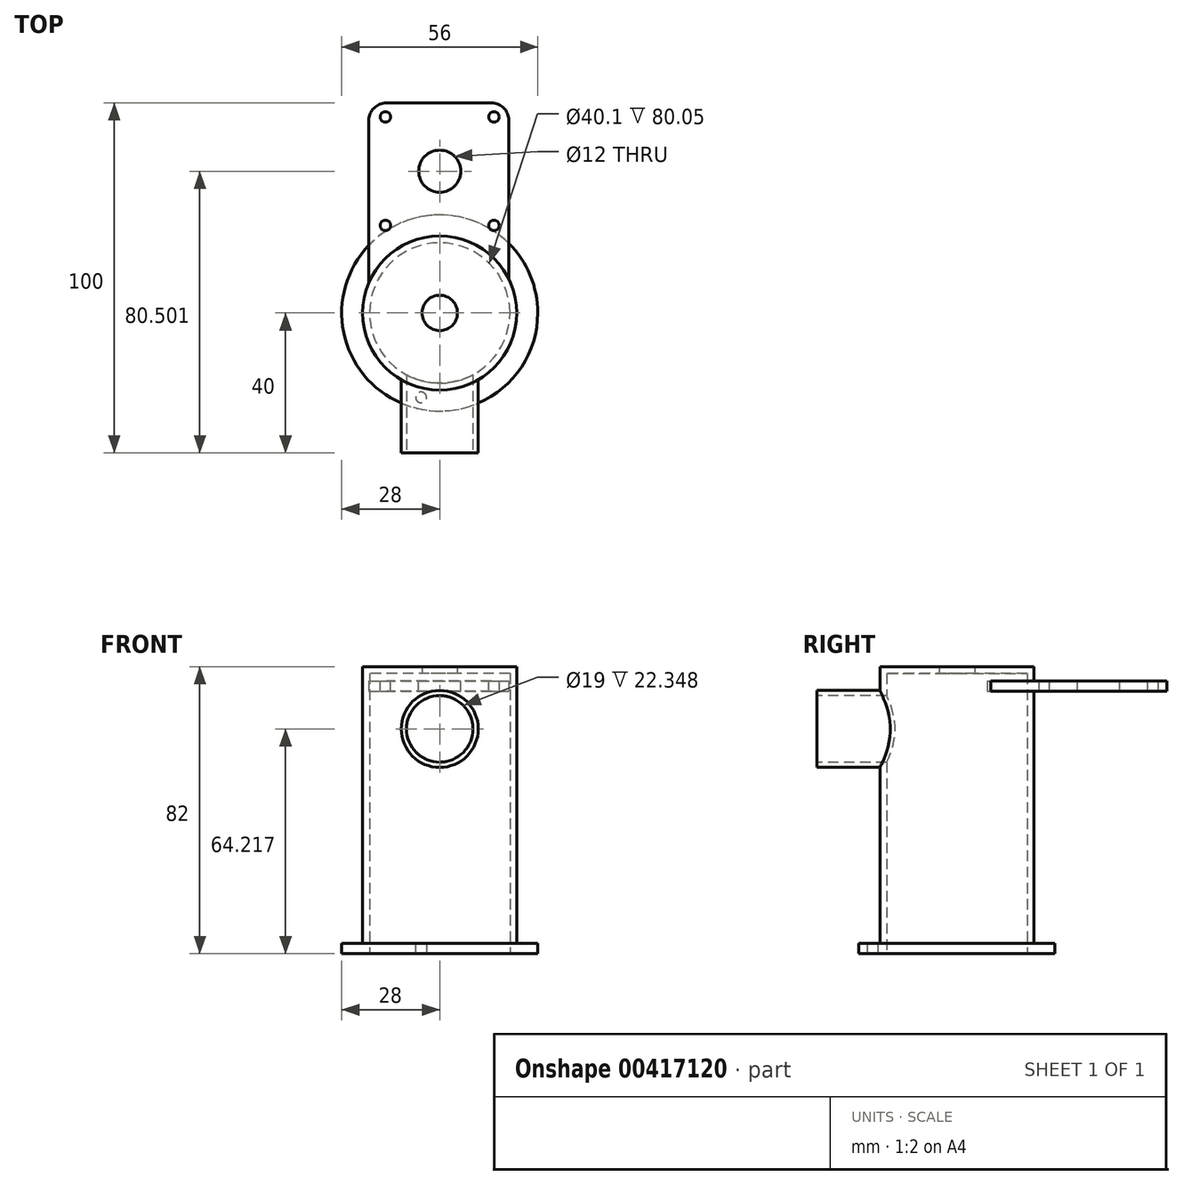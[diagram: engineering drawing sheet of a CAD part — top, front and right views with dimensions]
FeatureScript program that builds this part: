
annotation { "Feature Type Name" : "Feature", "Feature Type Description" : "" }
export const myFeature = defineFeature(function(context is Context, id is Id, definition is map)
    precondition{}
    {
        {
            var Q0;
            Q0=qCreatedBy(makeId("Top.planeOp"),FACE);
            var sketch = newSketch(context, id + "F0", { "sketchPlane" : qUnion([Q0])});
            skCircle(sketch, "E0", {"center": v(0, 0) * mm, "radius": 22 * mm});
            skCircle(sketch, "E1", {"center": v(0, 0) * mm, "radius": 28 * mm});
            skSolve(sketch);
        }
        {
            var Q0;
            Q0=makeQuery(id+"F0.imprint","IMPRINT",FACE,{"disambiguationData":[TD([[makeQuery(id+"F0.imprint","IMPRINT",EDGE,{"derivedFrom":sQuery(id+"F0.wireOp",EDGE,"E0")}),1.0]])]});
            extrude(context, id + "F1", {"entities" : qUnion([Q0]), "depth" : 82 * mm});
        }
        {
            var Q0;
            Q0=makeQuery(id+"F1.opExtrude","CAP_FACE",FACE,{"disambiguationData":[OSD([sQuery(id+"F0.wireOp",EDGE,"E0")])],"isStart":true});
            shell(context, id + "F2", {"entities" : qUnion([Q0]), "thickness" : 1.95 * mm});
        }
        {
            var Q0;
            Q0=makeQuery(id+"F0.imprint","IMPRINT",FACE,{"disambiguationData":[TD([[makeQuery(id+"F0.imprint","IMPRINT",EDGE,{"derivedFrom":sQuery(id+"F0.wireOp",EDGE,"E0")}),-1.0]])]});
            extrude(context, id + "F3", {"entities" : qUnion([Q0]), "operationType" : NewBodyOperationType.ADD, "depth" : 3 * mm});
        }
        {
            var Q0;
            Q0=qCreatedBy(makeId("Front.planeOp"),FACE);
            var sketch = newSketch(context, id + "F4", { "sketchPlane" : qUnion([Q0])});
            skLineSegment(sketch, "E2", {"start": v(0, -30.48) * mm, "end": v(0, 118.91) * mm, "construction": true});
            skSolve(sketch);
        }
        {
            var Q0;
            Q0=qCreatedBy(makeId("Top.planeOp"),FACE);
            var sketch = newSketch(context, id + "F5", { "sketchPlane" : qUnion([Q0])});
            skCircle(sketch, "E3", {"center": v(0, 0) * mm, "radius": 5.05 * mm});
            skSolve(sketch);
        }
        {
            var Q0;
            Q0 = qSketchRegion(id + "F5", true);
            extrude(context, id + "F6", {"entities" : qUnion([Q0]), "operationType" : NewBodyOperationType.REMOVE, "depth" : 90 * mm});
        }
        {
            var Q0;
            Q0=makeQuery(id+"F0.imprint","IMPRINT",FACE,{"disambiguationData":[TD([[makeQuery(id+"F0.imprint","IMPRINT",EDGE,{"derivedFrom":sQuery(id+"F0.wireOp",EDGE,"E0")}),-1.0]])]});
            var sketch = newSketch(context, id + "F7", { "sketchPlane" : qUnion([Q0])});
            skCircle(sketch, "E4", {"center": v(-5.33, -24.1) * mm, "radius": 1.55 * mm});
            skSolve(sketch);
        }
        {
            var Q0;
            Q0 = qSketchRegion(id + "F7", true);
            extrude(context, id + "F8", {"entities" : qUnion([Q0]), "operationType" : NewBodyOperationType.REMOVE, "depth" : 5 * mm});
        }
        {
            var Q0;
            Q0=qCreatedBy(makeId("Front.planeOp"),FACE);
            cPlane(context, id + "F9", {"entities" : qUnion([Q0]), "cplaneType" : CPlaneType.OFFSET, "offset" : 40 * mm, "width" : 150 * mm, "height" : 150 * mm});
        }
        {
            var Q0;
            Q0=qCreatedBy(id+"F9.planeOp",FACE);
            var sketch = newSketch(context, id + "F10", { "sketchPlane" : qUnion([Q0])});
            skCircle(sketch, "E5", {"center": v(0, 64.22) * mm, "radius": 11 * mm});
            skSolve(sketch);
        }
        {
            var Q0;
            Q0=makeQuery(id+"F10.imprint","IMPRINT",FACE,{"disambiguationData":[TD([[makeQuery(id+"F10.imprint","IMPRINT",EDGE,{"derivedFrom":sQuery(id+"F10.wireOp",EDGE,"E5")}),1.0]])]});
            extrude(context, id + "F11", {"entities" : qUnion([Q0]), "operationType" : NewBodyOperationType.ADD, "endBound" : BoundingType.UP_TO_NEXT, "oppositeDirection" : true, "depth" : 25 * mm});
        }
        {
            var Q0;
            Q0=makeQuery(id+"F11.opExtrude","CAP_FACE",FACE,{"disambiguationData":[OSD([sQuery(id+"F10.wireOp",EDGE,"E5")])],"isStart":true});
            var sketch = newSketch(context, id + "F12", { "sketchPlane" : qUnion([Q0])});
            skCircle(sketch, "E6", {"center": v(0, 64.22) * mm, "radius": 9.5 * mm});
            skSolve(sketch);
        }
        {
            var Q0;
            Q0 = qSketchRegion(id + "F12", true);
            extrude(context, id + "F13", {"entities" : qUnion([Q0]), "operationType" : NewBodyOperationType.REMOVE, "oppositeDirection" : true, "depth" : 30 * mm});
        }
        {
            var Q0;
            Q0=qCreatedBy(makeId("Front.planeOp"),FACE);
            cPlane(context, id + "F14", {"entities" : qUnion([Q0]), "cplaneType" : CPlaneType.OFFSET, "offset" : 60 * mm, "oppositeDirection" : true, "width" : 150 * mm, "height" : 150 * mm});
        }
        {
            var Q0;
            Q0=qCreatedBy(id+"F14.planeOp",FACE);
            var sketch = newSketch(context, id + "F15", { "sketchPlane" : qUnion([Q0])});
            skLineSegment(sketch, "E7.bottom", {"start": v(19.76, 74.93) * mm, "end": v(-20.24, 74.93) * mm});
            skLineSegment(sketch, "E7.top", {"start": v(19.76, 77.93) * mm, "end": v(-20.24, 77.93) * mm});
            skLineSegment(sketch, "E7.left", {"start": v(19.76, 74.93) * mm, "end": v(19.76, 77.93) * mm});
            skLineSegment(sketch, "E7.right", {"start": v(-20.24, 74.93) * mm, "end": v(-20.24, 77.93) * mm});
            skSolve(sketch);
        }
        {
            var Q0;
            Q0 = qSketchRegion(id + "F15", true);
            extrude(context, id + "F16", {"entities" : qUnion([Q0]), "operationType" : NewBodyOperationType.ADD, "endBound" : BoundingType.UP_TO_NEXT, "depth" : 25 * mm});
        }
        {
            var Q0;
            Q0=makeQuery(id+"F1.opExtrude","CAP_FACE",FACE,{"disambiguationData":[OSD([sQuery(id+"F0.wireOp",EDGE,"E0")])],"isStart":false});
            var sketch = newSketch(context, id + "F17", { "sketchPlane" : qUnion([Q0])});
            skLineSegment(sketch, "E8", {"start": v(0, 40.5) * mm, "end": v(0, 0) * mm, "construction": true});
            skLineSegment(sketch, "E9", {"start": v(-19.3, 21.76) * mm, "end": v(18.59, 59.64) * mm, "construction": true});
            skLineSegment(sketch, "E10.bottom", {"start": v(15.5, 25) * mm, "end": v(-15.5, 25) * mm});
            skLineSegment(sketch, "E10.top", {"start": v(15.5, 56) * mm, "end": v(-15.5, 56) * mm});
            skLineSegment(sketch, "E10.left", {"start": v(15.5, 25) * mm, "end": v(15.5, 56) * mm});
            skLineSegment(sketch, "E10.right", {"start": v(-15.5, 25) * mm, "end": v(-15.5, 56) * mm});
            skPoint(sketch, "E10.middle", {"position": v(0, 40.5) * mm});
            skCircle(sketch, "E11", {"center": v(-15.5, 56) * mm, "radius": 1.5 * mm});
            skCircle(sketch, "E12", {"center": v(15.5, 56) * mm, "radius": 1.5 * mm});
            skCircle(sketch, "E13", {"center": v(-15.5, 25) * mm, "radius": 1.5 * mm});
            skCircle(sketch, "E14", {"center": v(15.5, 25) * mm, "radius": 1.5 * mm});
            skCircle(sketch, "E15", {"center": v(0, 40.5) * mm, "radius": 6 * mm});
            skSolve(sketch);
        }
        {
            var Q0;
            {var subQ0=sQuery(id+"F17.wireOp",EDGE,"E10.left");var subQ1=sQuery(id+"F17.wireOp",EDGE,"E10.top");var subQ2=makeQuery(id+"F17.imprint","INTERSECT",VERTEX,{"derivedFrom":[subQ1,subQ0]});Q0=makeQuery(id+"F17.imprint","IMPRINT",FACE,{"disambiguationData":[TD([[makeQuery(id+"F17.imprint","IMPRINT",EDGE,{"disambiguationData":[TD([[subQ2,-1.0]])],"derivedFrom":subQ1}),-1.0]])]});}
            var Q1;
            {var subQ0=sQuery(id+"F17.wireOp",EDGE,"E10.left");var subQ1=sQuery(id+"F17.wireOp",EDGE,"E10.top");var subQ2=makeQuery(id+"F17.imprint","INTERSECT",VERTEX,{"derivedFrom":[subQ1,subQ0]});Q1=makeQuery(id+"F17.imprint","IMPRINT",FACE,{"disambiguationData":[TD([[makeQuery(id+"F17.imprint","IMPRINT",EDGE,{"disambiguationData":[TD([[subQ2,-1.0]])],"derivedFrom":subQ1}),1.0]])]});}
            var Q2;
            {var subQ0=sQuery(id+"F17.wireOp",EDGE,"E10.right");var subQ1=sQuery(id+"F17.wireOp",EDGE,"E10.top");var subQ2=makeQuery(id+"F17.imprint","INTERSECT",VERTEX,{"derivedFrom":[subQ1,subQ0]});Q2=makeQuery(id+"F17.imprint","IMPRINT",FACE,{"disambiguationData":[TD([[makeQuery(id+"F17.imprint","IMPRINT",EDGE,{"disambiguationData":[TD([[subQ2,1.0]])],"derivedFrom":subQ1}),-1.0]])]});}
            var Q3;
            {var subQ0=sQuery(id+"F17.wireOp",EDGE,"E10.right");var subQ1=sQuery(id+"F17.wireOp",EDGE,"E10.top");var subQ2=makeQuery(id+"F17.imprint","INTERSECT",VERTEX,{"derivedFrom":[subQ1,subQ0]});Q3=makeQuery(id+"F17.imprint","IMPRINT",FACE,{"disambiguationData":[TD([[makeQuery(id+"F17.imprint","IMPRINT",EDGE,{"disambiguationData":[TD([[subQ2,1.0]])],"derivedFrom":subQ1}),1.0]])]});}
            var Q4;
            {var subQ0=sQuery(id+"F17.wireOp",EDGE,"E10.right");var subQ1=sQuery(id+"F17.wireOp",EDGE,"E10.bottom");var subQ2=makeQuery(id+"F17.imprint","INTERSECT",VERTEX,{"derivedFrom":[subQ1,subQ0]});Q4=makeQuery(id+"F17.imprint","IMPRINT",FACE,{"disambiguationData":[TD([[makeQuery(id+"F17.imprint","IMPRINT",EDGE,{"disambiguationData":[TD([[subQ2,1.0]])],"derivedFrom":subQ1}),1.0]])]});}
            var Q5;
            {var subQ0=sQuery(id+"F17.wireOp",EDGE,"E10.right");var subQ1=sQuery(id+"F17.wireOp",EDGE,"E10.bottom");var subQ2=makeQuery(id+"F17.imprint","INTERSECT",VERTEX,{"derivedFrom":[subQ1,subQ0]});Q5=makeQuery(id+"F17.imprint","IMPRINT",FACE,{"disambiguationData":[TD([[makeQuery(id+"F17.imprint","IMPRINT",EDGE,{"disambiguationData":[TD([[subQ2,1.0]])],"derivedFrom":subQ1}),-1.0]])]});}
            var Q6;
            {var subQ0=sQuery(id+"F17.wireOp",EDGE,"E10.left");var subQ1=sQuery(id+"F17.wireOp",EDGE,"E10.bottom");var subQ2=makeQuery(id+"F17.imprint","INTERSECT",VERTEX,{"derivedFrom":[subQ1,subQ0]});Q6=makeQuery(id+"F17.imprint","IMPRINT",FACE,{"disambiguationData":[TD([[makeQuery(id+"F17.imprint","IMPRINT",EDGE,{"disambiguationData":[TD([[subQ2,-1.0]])],"derivedFrom":subQ1}),1.0]])]});}
            var Q7;
            {var subQ0=sQuery(id+"F17.wireOp",EDGE,"E10.left");var subQ1=sQuery(id+"F17.wireOp",EDGE,"E10.bottom");var subQ2=makeQuery(id+"F17.imprint","INTERSECT",VERTEX,{"derivedFrom":[subQ1,subQ0]});Q7=makeQuery(id+"F17.imprint","IMPRINT",FACE,{"disambiguationData":[TD([[makeQuery(id+"F17.imprint","IMPRINT",EDGE,{"disambiguationData":[TD([[subQ2,-1.0]])],"derivedFrom":subQ1}),-1.0]])]});}
            var Q8;
            Q8=makeQuery(id+"F17.imprint","IMPRINT",FACE,{"disambiguationData":[TD([[makeQuery(id+"F17.imprint","IMPRINT",EDGE,{"derivedFrom":sQuery(id+"F17.wireOp",EDGE,"E15")}),1.0]])]});
            extrude(context, id + "F18", {"entities" : qUnion([Q0, Q1, Q2, Q3, Q4, Q5, Q6, Q7, Q8]), "operationType" : NewBodyOperationType.REMOVE, "oppositeDirection" : true, "depth" : 10 * mm});
        }
        {
            var Q0;
            Q0=makeQuery(id+"F16.opExtrude","CAP_EDGE",EDGE,{"disambiguationData":[OSD([sQuery(id+"F15.wireOp",EDGE,"E7.right")])],"isStart":true});
            var Q1;
            Q1=makeQuery(id+"F16.opExtrude","CAP_EDGE",EDGE,{"disambiguationData":[OSD([sQuery(id+"F15.wireOp",EDGE,"E7.left")])],"isStart":true});
            fillet(context, id + "F19", {"entities" : qUnion([Q0, Q1]), "radius" : 5 * mm, "tangentPropagation" : true, "allowEdgeOverflow" : false});
        }
    });
